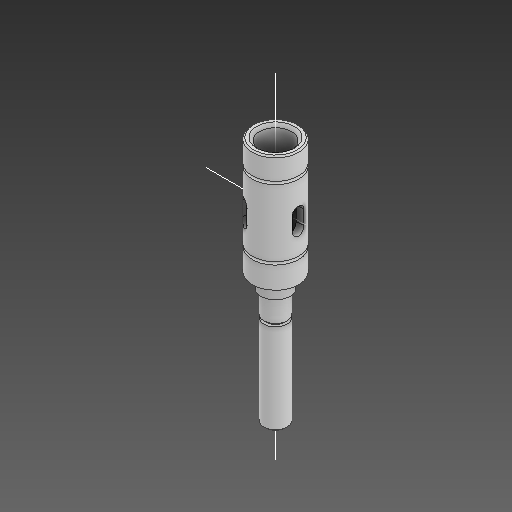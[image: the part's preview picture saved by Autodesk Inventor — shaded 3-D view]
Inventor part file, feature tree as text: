
AUTODESK INVENTOR PART (.ipt)
format: ipt  version: 2021 (Build 250183000, 183)  size: 217,088 bytes
history: native  units: in
note: dims shown in document units (in); Inventor stores cm internally (conversion verified against a paired STEP export)
features: sketch x9, other x8, plane x3
ambient origin geometry x8: Origin, YZ Plane, XZ Plane, XY Plane, X Axis, Y Axis, Z Axis, Center Point
bodies: Solid1 (feature_tree)
feature tree (20):
  other  "iner_sleeve.ipt"
  other  "Solid1::iner_sleeve.ipt"
  other  "TaggingFeature1"
  sketch  "Sketch1"  dims[d0=0.3937in]
  sketch  "Sketch2"
  sketch  "Sketch3"
  sketch  "Sketch5"
  sketch  "Sketch6"
  sketch  "Sketch7"
  sketch  "Sketch8"
  sketch  "Sketch10"
  sketch  "Sketch11"
  plane  "Work Plane1"
  plane  "Work Plane2"
  plane  "Work Plane3"
  other  "Work Axis1"
  other  "Work Axis2"
  other  "Work Axis3"
  other  "Srf1"
  other  "Srf1::Derived"
